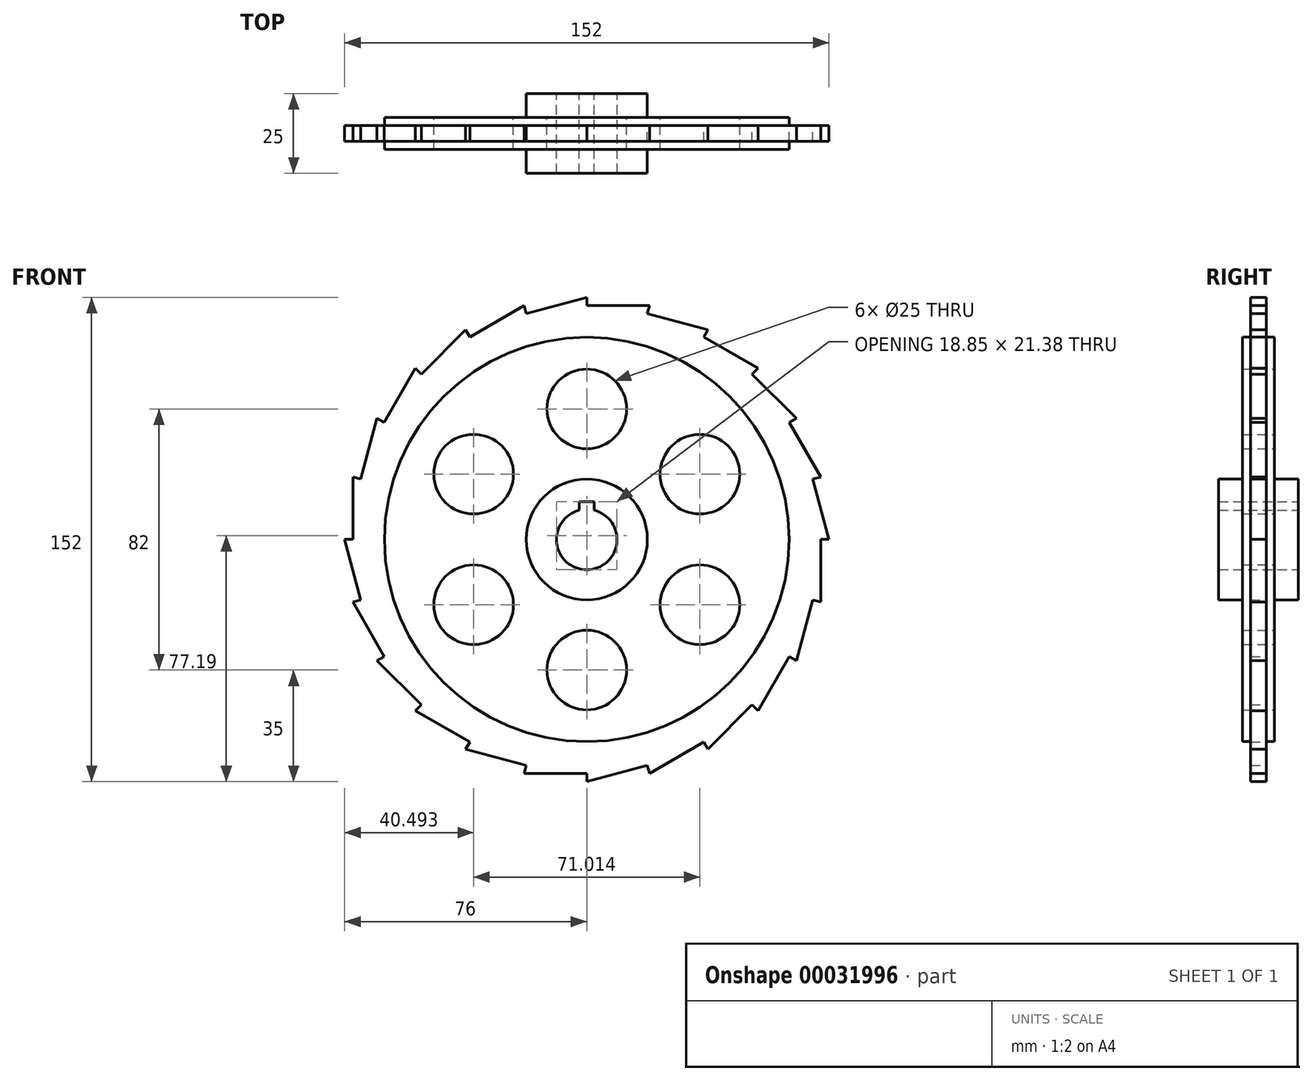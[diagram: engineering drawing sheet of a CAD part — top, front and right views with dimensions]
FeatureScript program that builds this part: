
annotation { "Feature Type Name" : "Feature", "Feature Type Description" : "" }
export const myFeature = defineFeature(function(context is Context, id is Id, definition is map)
    precondition{}
    {
        {
            var Q0;
            Q0=qCreatedBy(makeId("Front.planeOp"),FACE);
            var sketch = newSketch(context, id + "F0", { "sketchPlane" : qUnion([Q0])});
            skCircle(sketch, "E0", {"center": v(0, 0) * mm, "radius": 76 * mm, "construction": true});
            skLineSegment(sketch, "E1", {"start": v(70.9, 19) * mm, "end": v(73.41, 19.67) * mm});
            skLineSegment(sketch, "E2", {"start": v(0, 0) * mm, "end": v(76, 0) * mm, "construction": true});
            skLineSegment(sketch, "E3", {"start": v(76, 0) * mm, "end": v(70.9, 19) * mm});
            skLineSegment(sketch, "E4.1.0", {"start": v(73.41, 19.67) * mm, "end": v(63.58, 36.7) * mm});
            skLineSegment(sketch, "E4.1.1", {"start": v(63.58, 36.7) * mm, "end": v(65.82, 38) * mm});
            skLineSegment(sketch, "E4.2.0", {"start": v(65.82, 38) * mm, "end": v(51.9, 51.9) * mm});
            skLineSegment(sketch, "E4.2.1", {"start": v(51.9, 51.9) * mm, "end": v(53.74, 53.74) * mm});
            skLineSegment(sketch, "E4.3.0", {"start": v(53.74, 53.74) * mm, "end": v(36.7, 63.58) * mm});
            skLineSegment(sketch, "E4.3.1", {"start": v(36.7, 63.58) * mm, "end": v(38, 65.82) * mm});
            skLineSegment(sketch, "E4.4.0", {"start": v(38, 65.82) * mm, "end": v(19, 70.9) * mm});
            skLineSegment(sketch, "E4.4.1", {"start": v(19, 70.9) * mm, "end": v(19.67, 73.41) * mm});
            skLineSegment(sketch, "E4.5.0", {"start": v(19.67, 73.41) * mm, "end": v(0, 73.41) * mm});
            skLineSegment(sketch, "E4.5.1", {"start": v(0, 73.41) * mm, "end": v(0, 76) * mm});
            skLineSegment(sketch, "E4.6.0", {"start": v(0, 76) * mm, "end": v(-19, 70.9) * mm});
            skLineSegment(sketch, "E4.6.1", {"start": v(-19, 70.9) * mm, "end": v(-19.67, 73.41) * mm});
            skLineSegment(sketch, "E4.7.0", {"start": v(-19.67, 73.41) * mm, "end": v(-36.7, 63.58) * mm});
            skLineSegment(sketch, "E4.7.1", {"start": v(-36.7, 63.58) * mm, "end": v(-38, 65.82) * mm});
            skLineSegment(sketch, "E4.8.0", {"start": v(-38, 65.82) * mm, "end": v(-51.9, 51.9) * mm});
            skLineSegment(sketch, "E4.8.1", {"start": v(-51.9, 51.9) * mm, "end": v(-53.74, 53.74) * mm});
            skLineSegment(sketch, "E4.9.0", {"start": v(-53.74, 53.74) * mm, "end": v(-63.58, 36.7) * mm});
            skLineSegment(sketch, "E4.9.1", {"start": v(-63.58, 36.7) * mm, "end": v(-65.82, 38) * mm});
            skLineSegment(sketch, "E4.10.0", {"start": v(-65.82, 38) * mm, "end": v(-70.9, 19) * mm});
            skLineSegment(sketch, "E4.10.1", {"start": v(-70.9, 19) * mm, "end": v(-73.41, 19.67) * mm});
            skLineSegment(sketch, "E4.11.0", {"start": v(-73.41, 19.67) * mm, "end": v(-73.41, 0) * mm});
            skLineSegment(sketch, "E4.11.1", {"start": v(-73.41, 0) * mm, "end": v(-76, 0) * mm});
            skLineSegment(sketch, "E4.12.0", {"start": v(-76, 0) * mm, "end": v(-70.9, -19) * mm});
            skLineSegment(sketch, "E4.12.1", {"start": v(-70.9, -19) * mm, "end": v(-73.41, -19.67) * mm});
            skLineSegment(sketch, "E4.13.0", {"start": v(-73.41, -19.67) * mm, "end": v(-63.58, -36.7) * mm});
            skLineSegment(sketch, "E4.13.1", {"start": v(-63.58, -36.7) * mm, "end": v(-65.82, -38) * mm});
            skLineSegment(sketch, "E4.14.0", {"start": v(-65.82, -38) * mm, "end": v(-51.9, -51.9) * mm});
            skLineSegment(sketch, "E4.14.1", {"start": v(-51.9, -51.9) * mm, "end": v(-53.74, -53.74) * mm});
            skLineSegment(sketch, "E4.15.0", {"start": v(-53.74, -53.74) * mm, "end": v(-36.7, -63.58) * mm});
            skLineSegment(sketch, "E4.15.1", {"start": v(-36.7, -63.58) * mm, "end": v(-38, -65.82) * mm});
            skLineSegment(sketch, "E4.16.0", {"start": v(-38, -65.82) * mm, "end": v(-19, -70.9) * mm});
            skLineSegment(sketch, "E4.16.1", {"start": v(-19, -70.9) * mm, "end": v(-19.67, -73.41) * mm});
            skLineSegment(sketch, "E4.17.0", {"start": v(-19.67, -73.41) * mm, "end": v(0, -73.41) * mm});
            skLineSegment(sketch, "E4.17.1", {"start": v(0, -73.41) * mm, "end": v(0, -76) * mm});
            skLineSegment(sketch, "E4.18.0", {"start": v(0, -76) * mm, "end": v(19, -70.9) * mm});
            skLineSegment(sketch, "E4.18.1", {"start": v(19, -70.9) * mm, "end": v(19.67, -73.41) * mm});
            skLineSegment(sketch, "E4.19.0", {"start": v(19.67, -73.41) * mm, "end": v(36.7, -63.58) * mm});
            skLineSegment(sketch, "E4.19.1", {"start": v(36.7, -63.58) * mm, "end": v(38, -65.82) * mm});
            skLineSegment(sketch, "E4.20.0", {"start": v(38, -65.82) * mm, "end": v(51.9, -51.9) * mm});
            skLineSegment(sketch, "E4.20.1", {"start": v(51.9, -51.9) * mm, "end": v(53.74, -53.74) * mm});
            skLineSegment(sketch, "E4.21.0", {"start": v(53.74, -53.74) * mm, "end": v(63.58, -36.7) * mm});
            skLineSegment(sketch, "E4.21.1", {"start": v(63.58, -36.7) * mm, "end": v(65.82, -38) * mm});
            skLineSegment(sketch, "E4.22.0", {"start": v(65.82, -38) * mm, "end": v(70.9, -19) * mm});
            skLineSegment(sketch, "E4.22.1", {"start": v(70.9, -19) * mm, "end": v(73.41, -19.67) * mm});
            skLineSegment(sketch, "E4.23.0", {"start": v(73.41, -19.67) * mm, "end": v(73.41, 0) * mm});
            skLineSegment(sketch, "E4.23.1", {"start": v(73.41, 0) * mm, "end": v(76, 0) * mm});
            skCircle(sketch, "E5", {"center": v(0, 0) * mm, "radius": 63.5 * mm});
            skSolve(sketch);
        }
        {
            var Q0;
            Q0=makeQuery(id+"F0.imprint","IMPRINT",FACE,{"disambiguationData":[TD([[makeQuery(id+"F0.imprint","IMPRINT",EDGE,{"derivedFrom":sQuery(id+"F0.wireOp",EDGE,"E1")}),1.0]])]});
            extrude(context, id + "F1", {"entities" : qUnion([Q0]), "endBound" : BoundingType.SYMMETRIC, "depth" : 5 * mm});
        }
        {
            var Q0;
            Q0=qCreatedBy(makeId("Front.planeOp"),FACE);
            var sketch = newSketch(context, id + "F2", { "sketchPlane" : qUnion([Q0])});
            skCircle(sketch, "E6", {"center": v(0, 0) * mm, "radius": 63.5 * mm});
            skCircle(sketch, "E7", {"center": v(0, 0) * mm, "radius": 19 * mm});
            skCircle(sketch, "E8", {"center": v(0, 41) * mm, "radius": 12.5 * mm});
            skCircle(sketch, "E9.1.0", {"center": v(-35.5, 20.5) * mm, "radius": 12.5 * mm});
            skCircle(sketch, "E9.2.0", {"center": v(-35.5, -20.5) * mm, "radius": 12.5 * mm});
            skCircle(sketch, "E9.3.0", {"center": v(0, -41) * mm, "radius": 12.5 * mm});
            skCircle(sketch, "E9.4.0", {"center": v(35.5, -20.5) * mm, "radius": 12.5 * mm});
            skCircle(sketch, "E9.5.0", {"center": v(35.5, 20.5) * mm, "radius": 12.5 * mm});
            skSolve(sketch);
        }
        {
            var Q0;
            Q0=makeQuery(id+"F2.imprint","IMPRINT",FACE,{"disambiguationData":[TD([[makeQuery(id+"F2.imprint","IMPRINT",EDGE,{"derivedFrom":sQuery(id+"F2.wireOp",EDGE,"E6")}),1.0]])]});
            extrude(context, id + "F3", {"entities" : qUnion([Q0]), "operationType" : NewBodyOperationType.ADD, "endBound" : BoundingType.SYMMETRIC, "depth" : 10 * mm});
        }
        {
            var Q0;
            Q0=qCreatedBy(makeId("Front.planeOp"),FACE);
            var sketch = newSketch(context, id + "F4", { "sketchPlane" : qUnion([Q0])});
            skCircle(sketch, "E10", {"center": v(0, 0) * mm, "radius": 19 * mm});
            skCircle(sketch, "E11", {"center": v(0, 0) * mm, "radius": 9.5 * mm});
            skLineSegment(sketch, "E12", {"start": v(0, 9.5) * mm, "end": v(0, 11.88) * mm});
            skLineSegment(sketch, "E13", {"start": v(0, 11.88) * mm, "end": v(2.38, 11.88) * mm});
            skLineSegment(sketch, "E14", {"start": v(2.38, 11.88) * mm, "end": v(2.38, 9.2) * mm});
            skLineSegment(sketch, "E15", {"start": v(0, 11.88) * mm, "end": v(-2.38, 11.88) * mm});
            skLineSegment(sketch, "E16", {"start": v(-2.38, 11.88) * mm, "end": v(-2.38, 9.2) * mm});
            skSolve(sketch);
        }
        {
            var Q0;
            Q0=makeQuery(id+"F4.imprint","IMPRINT",FACE,{"disambiguationData":[TD([[makeQuery(id+"F4.imprint","IMPRINT",EDGE,{"derivedFrom":sQuery(id+"F4.wireOp",EDGE,"E10")}),1.0]])]});
            extrude(context, id + "F5", {"entities" : qUnion([Q0]), "operationType" : NewBodyOperationType.ADD, "endBound" : BoundingType.SYMMETRIC, "depth" : 25 * mm});
        }
    });
